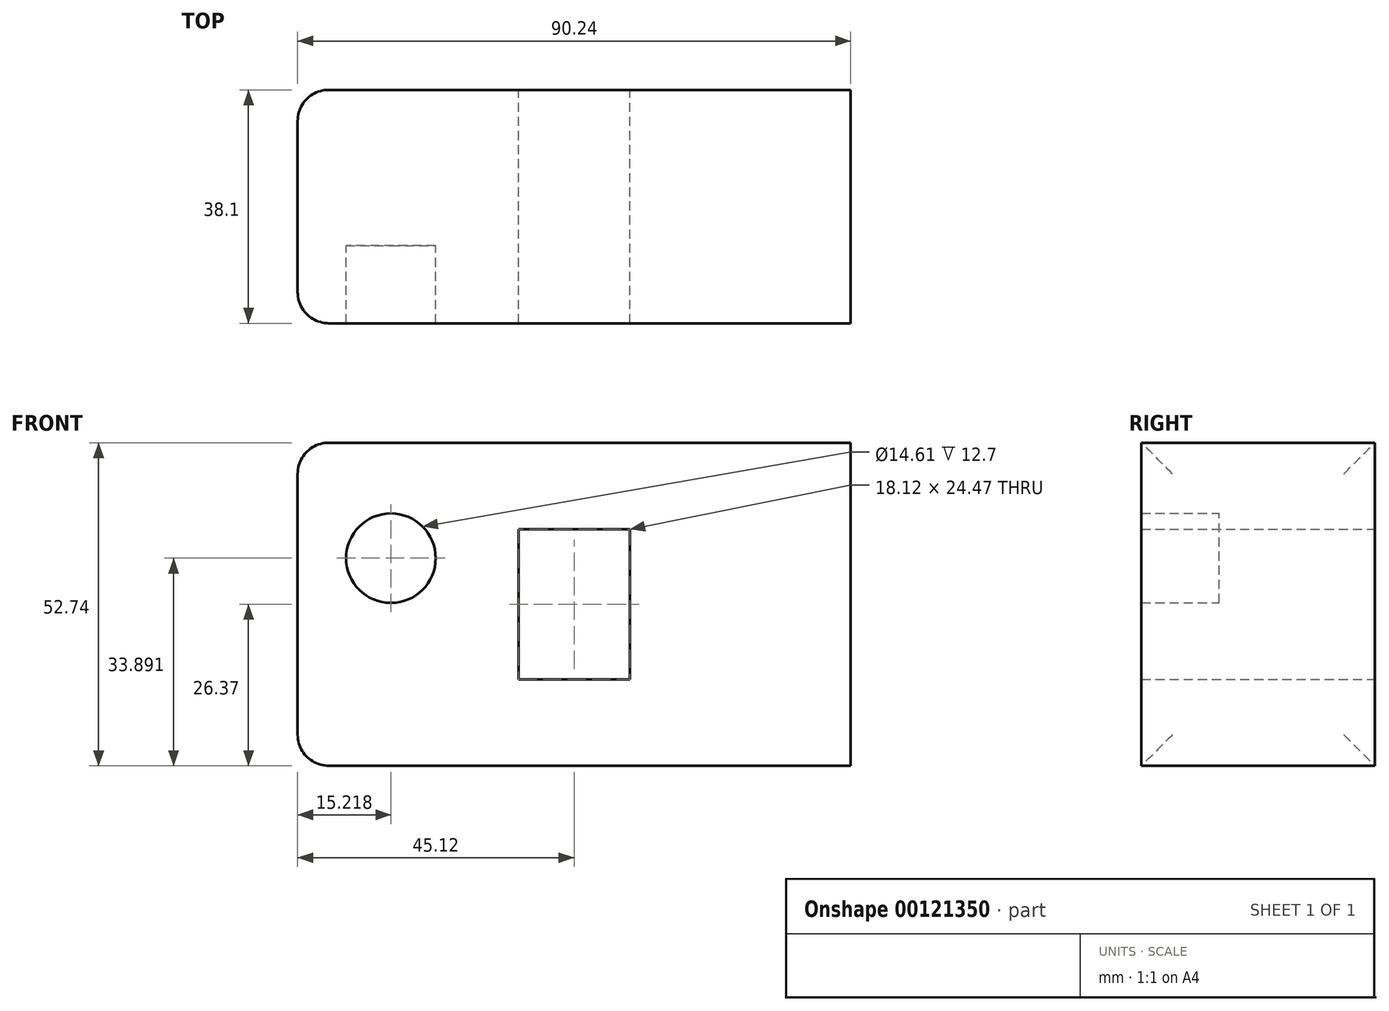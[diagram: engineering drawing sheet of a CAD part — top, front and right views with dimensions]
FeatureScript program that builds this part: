
annotation { "Feature Type Name" : "Feature", "Feature Type Description" : "" }
export const myFeature = defineFeature(function(context is Context, id is Id, definition is map)
    precondition{}
    {
        {
            var Q0;
            Q0=qCreatedBy(makeId("Front.planeOp"),FACE);
            var sketch = newSketch(context, id + "F0", { "sketchPlane" : qUnion([Q0])});
            skLineSegment(sketch, "E0.bottom", {"start": v(-45.12, 26.37) * mm, "end": v(45.12, 26.37) * mm});
            skLineSegment(sketch, "E0.top", {"start": v(-45.12, -26.37) * mm, "end": v(45.12, -26.37) * mm});
            skLineSegment(sketch, "E0.left", {"start": v(-45.12, 26.37) * mm, "end": v(-45.12, -26.37) * mm});
            skLineSegment(sketch, "E0.right", {"start": v(45.12, 26.37) * mm, "end": v(45.12, -26.37) * mm});
            skPoint(sketch, "E0.middle", {"position": v(0, 0) * mm});
            skLineSegment(sketch, "E1.bottom", {"start": v(-9.06, -12.23) * mm, "end": v(9.06, -12.23) * mm});
            skLineSegment(sketch, "E1.top", {"start": v(-9.06, 12.23) * mm, "end": v(9.06, 12.23) * mm});
            skLineSegment(sketch, "E1.left", {"start": v(-9.06, -12.23) * mm, "end": v(-9.06, 12.23) * mm});
            skLineSegment(sketch, "E1.right", {"start": v(9.06, -12.23) * mm, "end": v(9.06, 12.23) * mm});
            skSolve(sketch);
        }
        {
            var Q0;
            Q0=makeQuery(id+"F0.imprint","IMPRINT",FACE,{"disambiguationData":[TD([[makeQuery(id+"F0.imprint","IMPRINT",EDGE,{"derivedFrom":sQuery(id+"F0.wireOp",EDGE,"E0.bottom")}),-1.0]])]});
            extrude(context, id + "F1", {"entities" : qUnion([Q0]), "endBound" : BoundingType.SYMMETRIC, "depth" : 25.4 * mm});
        }
        {
            var Q0;
            Q0=makeQuery(id+"F1.opExtrude","CAP_FACE",FACE,{"disambiguationData":[OSD([sQuery(id+"F0.wireOp",EDGE,"E0.bottom"),sQuery(id+"F0.wireOp",EDGE,"E0.top"),sQuery(id+"F0.wireOp",EDGE,"E0.left"),sQuery(id+"F0.wireOp",EDGE,"E0.right"),sQuery(id+"F0.wireOp",EDGE,"E1.bottom"),sQuery(id+"F0.wireOp",EDGE,"E1.top"),sQuery(id+"F0.wireOp",EDGE,"E1.left"),sQuery(id+"F0.wireOp",EDGE,"E1.right")])],"isStart":false});
            var sketch = newSketch(context, id + "F2", { "sketchPlane" : qUnion([Q0])});
            skCircle(sketch, "E2", {"center": v(-29.9, 7.52) * mm, "radius": 7.3 * mm});
            skSolve(sketch);
        }
        {
            var Q0;
            Q0=makeQuery(id+"F2.imprint","IMPRINT",FACE,{"disambiguationData":[TD([[makeQuery(id+"F2.imprint","IMPRINT",EDGE,{"derivedFrom":sQuery(id+"F2.wireOp",EDGE,"E2")}),-1.0]])]});
            extrude(context, id + "F3", {"entities" : qUnion([Q0]), "operationType" : NewBodyOperationType.ADD, "endBound" : BoundingType.SYMMETRIC, "depth" : 25.4 * mm});
        }
        {
            var Q0;
            {var subQ0=sQuery(id+"F0.wireOp",EDGE,"E0.left");Q0=makeQuery(id+"F3.boolean.opBoolean","MERGE",FACE,{"derivedFrom":[makeQuery(id+"F1.opExtrude","SWEPT_FACE",FACE,{"disambiguationData":[OSD([subQ0])]}),makeQuery(id+"F3.opExtrude","SWEPT_FACE",FACE,{"disambiguationData":[OSD([subQ0])]})]});}
            fillet(context, id + "F4", {"entities" : qUnion([Q0]), "radius" : 5.08 * mm, "tangentPropagation" : true, "allowEdgeOverflow" : false});
        }
    });
